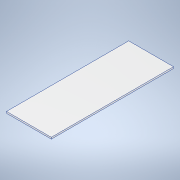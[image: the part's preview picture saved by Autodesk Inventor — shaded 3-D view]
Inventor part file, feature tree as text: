
AUTODESK INVENTOR PART (.ipt)
format: ipt  version: 2022 (Build 260153000, 153)  size: 93,696 bytes
history: native  units: mm
features: extrude x1, sketch x1
ambient origin geometry x8: Origin, YZ Plane, XZ Plane, XY Plane, X Axis, Y Axis, Z Axis, Center Point
bodies: Solid1 (feature_tree)
feature tree (2):
  extrude  "Extrusion1"  Depth=600.0mm
  sketch  "Sketch1"  dims[d0=220.0mm d1=600.0mm d2=8.0mm d3=0.0mm]
